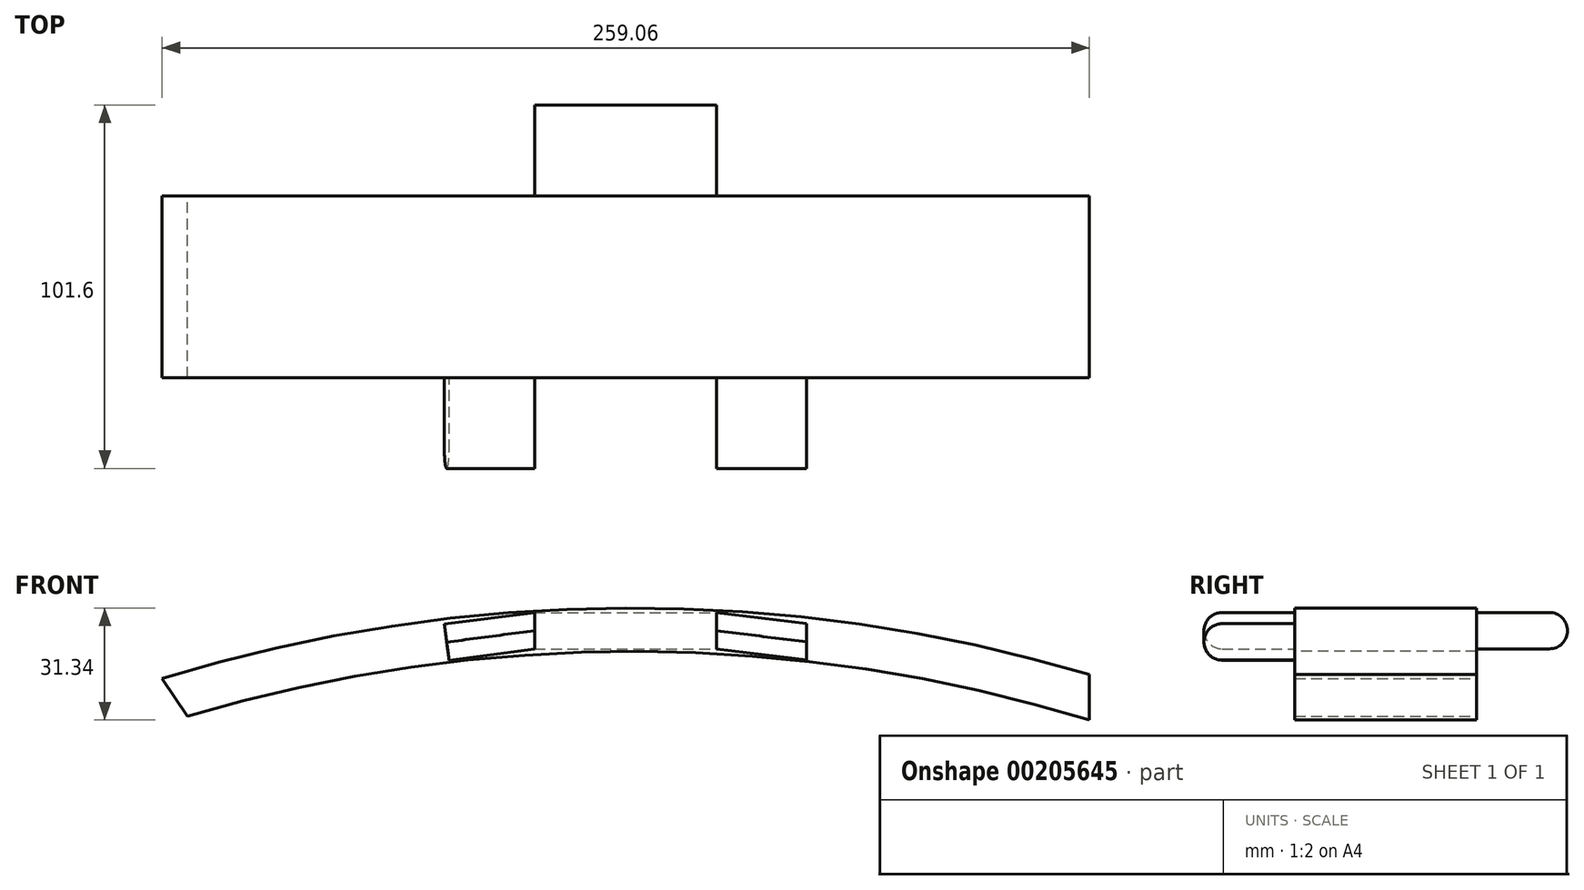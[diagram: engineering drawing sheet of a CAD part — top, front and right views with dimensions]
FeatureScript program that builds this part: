
annotation { "Feature Type Name" : "Feature", "Feature Type Description" : "" }
export const myFeature = defineFeature(function(context is Context, id is Id, definition is map)
    precondition{}
    {
        {
            var Q0;
            Q0=qCreatedBy(makeId("Right.planeOp"),FACE);
            var sketch = newSketch(context, id + "F0", { "sketchPlane" : qUnion([Q0])});
            skLineSegment(sketch, "E0.bottom", {"start": v(-25.4, 6.35) * mm, "end": v(25.4, 6.35) * mm});
            skLineSegment(sketch, "E0.top", {"start": v(-25.4, -6.35) * mm, "end": v(25.4, -6.35) * mm});
            skLineSegment(sketch, "E0.left", {"start": v(-25.4, 6.35) * mm, "end": v(-25.4, -6.35) * mm});
            skLineSegment(sketch, "E0.right", {"start": v(25.4, 6.35) * mm, "end": v(25.4, -6.35) * mm});
            skPoint(sketch, "E0.middle", {"position": v(0, 0) * mm});
            skSolve(sketch);
        }
        {
            var Q0;
            Q0=qCreatedBy(makeId("Front.planeOp"),FACE);
            var sketch = newSketch(context, id + "F1", { "sketchPlane" : qUnion([Q0])});
            skArc(sketch, "E1", {"start": v(0, 0) * mm, "mid": v(-127.77, 18.91) * mm, "end": v(-255.54, 0) * mm});
            skSolve(sketch);
        }
        {
            var Q0;
            Q0=makeQuery(id+"F0.imprint","IMPRINT",FACE,{"disambiguationData":[TD([[makeQuery(id+"F0.imprint","IMPRINT",EDGE,{"derivedFrom":sQuery(id+"F0.wireOp",EDGE,"E0.bottom")}),-1.0]])]});
            var Q1;
            Q1=sQuery(id+"F1.wireOp",EDGE,"E1");
            sweep(context, id + "F2", {"profiles" : qUnion([Q0]), "path" : qUnion([Q1])});
        }
        {
            var Q0;
            Q0=makeQuery(id+"F2.opSweep","SWEPT_FACE",FACE,{"disambiguationData":[OSD([sQuery(id+"F0.wireOp",EDGE,"E0.right"),sQuery(id+"F1.wireOp",EDGE,"E1")])]});
            var sketch = newSketch(context, id + "F3", { "sketchPlane" : qUnion([Q0])});
            skLineSegment(sketch, "E2", {"start": v(129.6, 25) * mm, "end": v(129.6, 12.3) * mm});
            skLineSegment(sketch, "E3.bottom", {"start": v(155, 13.56) * mm, "end": v(104.2, 13.56) * mm});
            skLineSegment(sketch, "E3.top", {"start": v(155, 23.72) * mm, "end": v(104.2, 23.72) * mm});
            skLineSegment(sketch, "E3.left", {"start": v(155, 13.56) * mm, "end": v(155, 23.72) * mm});
            skLineSegment(sketch, "E3.right", {"start": v(104.2, 13.56) * mm, "end": v(104.2, 23.72) * mm});
            skPoint(sketch, "E3.middle", {"position": v(129.6, 18.64) * mm});
            skSolve(sketch);
        }
        {
            var Q0;
            {var subQ5=sQuery(id+"F3.wireOp",EDGE,"E3.right");Q0=makeQuery(id+"F3.imprint","IMPRINT",FACE,{"disambiguationData":[TD([[makeQuery(id+"F3.imprint","IMPRINT",EDGE,{"derivedFrom":subQ5}),-1.0]])]});}
            var Q1;
            {var subQ5=sQuery(id+"F3.wireOp",EDGE,"E3.left");Q1=makeQuery(id+"F3.imprint","IMPRINT",FACE,{"disambiguationData":[TD([[makeQuery(id+"F3.imprint","IMPRINT",EDGE,{"derivedFrom":subQ5}),1.0]])]});}
            extrude(context, id + "F4", {"entities" : qUnion([Q0, Q1]), "operationType" : NewBodyOperationType.ADD, "depth" : 25.4 * mm});
        }
        {
            var Q0;
            Q0=makeQuery(id+"F4.opExtrude","CAP_EDGE",EDGE,{"disambiguationData":[OSD([sQuery(id+"F3.wireOp",EDGE,"E3.bottom")])],"isStart":false});
            var Q1;
            Q1=makeQuery(id+"F4.opExtrude","CAP_EDGE",EDGE,{"disambiguationData":[OSD([sQuery(id+"F3.wireOp",EDGE,"E3.top")])],"isStart":false});
            var Q2;
            Q2=makeQuery(id+"F4.opExtrude","CAP_EDGE",EDGE,{"disambiguationData":[OSD([sQuery(id+"F3.wireOp",EDGE,"E3.top")])],"isStart":true});
            var Q3;
            Q3=makeQuery(id+"F4.opExtrude","CAP_EDGE",EDGE,{"disambiguationData":[OSD([sQuery(id+"F3.wireOp",EDGE,"E3.bottom")])],"isStart":true});
            fillet(context, id + "F5", {"entities" : qUnion([Q0, Q1, Q2, Q3]), "radius" : 5.08 * mm, "tangentPropagation" : true, "allowEdgeOverflow" : false});
        }
        {
            var Q0;
            Q0=makeQuery(id+"F2.opSweep","SWEPT_FACE",FACE,{"disambiguationData":[OSD([sQuery(id+"F0.wireOp",EDGE,"E0.left"),sQuery(id+"F1.wireOp",EDGE,"E1")])]});
            var sketch = newSketch(context, id + "F6", { "sketchPlane" : qUnion([Q0])});
            skLineSegment(sketch, "E4", {"start": v(-129.6, 25) * mm, "end": v(-129.6, 12.3) * mm, "construction": true});
            skLineSegment(sketch, "E5.bottom", {"start": v(-104.2, 13.56) * mm, "end": v(-155, 13.56) * mm, "construction": true});
            skLineSegment(sketch, "E5.top", {"start": v(-104.2, 23.72) * mm, "end": v(-155, 23.72) * mm, "construction": true});
            skLineSegment(sketch, "E5.left", {"start": v(-104.2, 13.56) * mm, "end": v(-104.2, 23.72) * mm, "construction": true});
            skLineSegment(sketch, "E5.right", {"start": v(-155, 13.56) * mm, "end": v(-155, 23.72) * mm, "construction": true});
            skPoint(sketch, "E5.middle", {"position": v(-129.6, 18.64) * mm});
            skLineSegment(sketch, "E6", {"start": v(-104.2, 23.72) * mm, "end": v(-104.2, 13.56) * mm});
            skLineSegment(sketch, "E7", {"start": v(-155, 23.72) * mm, "end": v(-155, 13.56) * mm});
            skLineSegment(sketch, "E8", {"start": v(-104.2, 23.72) * mm, "end": v(-79, 20.6) * mm});
            skLineSegment(sketch, "E9", {"start": v(-79, 20.6) * mm, "end": v(-79, 10.43) * mm});
            skLineSegment(sketch, "E10", {"start": v(-79, 10.43) * mm, "end": v(-104.2, 13.56) * mm});
            skLineSegment(sketch, "E11", {"start": v(-155, 23.72) * mm, "end": v(-180.2, 20.47) * mm});
            skLineSegment(sketch, "E12", {"start": v(-180.2, 20.47) * mm, "end": v(-178.9, 10.4) * mm});
            skLineSegment(sketch, "E13", {"start": v(-178.9, 10.4) * mm, "end": v(-155, 13.56) * mm});
            skSolve(sketch);
        }
        {
            var Q0;
            Q0=makeQuery(id+"F6.imprint","IMPRINT",FACE,{"disambiguationData":[TD([[makeQuery(id+"F6.imprint","IMPRINT",EDGE,{"derivedFrom":sQuery(id+"F6.wireOp",EDGE,"E7")}),-1.0]])]});
            var Q1;
            Q1=makeQuery(id+"F6.imprint","IMPRINT",FACE,{"disambiguationData":[TD([[makeQuery(id+"F6.imprint","IMPRINT",EDGE,{"derivedFrom":sQuery(id+"F6.wireOp",EDGE,"E6")}),1.0]])]});
            extrude(context, id + "F7", {"entities" : qUnion([Q0, Q1]), "operationType" : NewBodyOperationType.ADD, "depth" : 25.4 * mm});
        }
        {
            var Q0;
            Q0=makeQuery(id+"F7.opExtrude","CAP_EDGE",EDGE,{"disambiguationData":[OSD([sQuery(id+"F6.wireOp",EDGE,"E11")])],"isStart":false});
            var Q1;
            Q1=makeQuery(id+"F7.opExtrude","CAP_EDGE",EDGE,{"disambiguationData":[OSD([sQuery(id+"F6.wireOp",EDGE,"E13")])],"isStart":false});
            var Q2;
            Q2=makeQuery(id+"F7.opExtrude","CAP_EDGE",EDGE,{"disambiguationData":[OSD([sQuery(id+"F6.wireOp",EDGE,"E10")])],"isStart":false});
            var Q3;
            Q3=makeQuery(id+"F7.opExtrude","CAP_EDGE",EDGE,{"disambiguationData":[OSD([sQuery(id+"F6.wireOp",EDGE,"E8")])],"isStart":true});
            var Q4;
            Q4=makeQuery(id+"F7.opExtrude","CAP_EDGE",EDGE,{"disambiguationData":[OSD([sQuery(id+"F6.wireOp",EDGE,"E8")])],"isStart":false});
            var Q5;
            Q5=makeQuery(id+"F7.opExtrude","CAP_EDGE",EDGE,{"disambiguationData":[OSD([sQuery(id+"F6.wireOp",EDGE,"E11")])],"isStart":true});
            var Q6;
            Q6=makeQuery(id+"F7.opExtrude","CAP_EDGE",EDGE,{"disambiguationData":[OSD([sQuery(id+"F6.wireOp",EDGE,"E13")])],"isStart":true});
            var Q7;
            Q7=makeQuery(id+"F7.opExtrude","CAP_EDGE",EDGE,{"disambiguationData":[OSD([sQuery(id+"F6.wireOp",EDGE,"E10")])],"isStart":true});
            var Q8;
            Q8=makeQuery(id+"F7.opExtrude","CAP_EDGE",EDGE,{"disambiguationData":[OSD([sQuery(id+"F6.wireOp",EDGE,"E9")])],"isStart":true});
            var Q9;
            Q9=makeQuery(id+"F7.opExtrude","CAP_EDGE",EDGE,{"disambiguationData":[OSD([sQuery(id+"F6.wireOp",EDGE,"E12")])],"isStart":true});
            fillet(context, id + "F8", {"entities" : qUnion([Q0, Q1, Q2, Q3, Q4, Q5, Q6, Q7, Q8, Q9]), "radius" : 5.08 * mm, "tangentPropagation" : true, "allowEdgeOverflow" : false});
        }
    });
